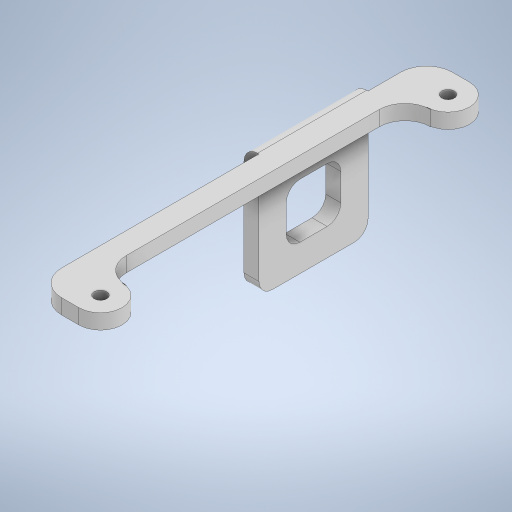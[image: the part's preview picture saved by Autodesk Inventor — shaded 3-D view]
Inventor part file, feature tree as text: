
AUTODESK INVENTOR PART (.ipt)
format: ipt  version: 2023 (Build 270158000, 158)  size: 672,256 bytes
history: native  units: in
note: dims shown in document units (in); Inventor stores cm internally (conversion verified against a paired STEP export)
features: extrude x3, sketch x3, fillet x1
ambient origin geometry x8: Origin, YZ Plane, XZ Plane, XY Plane, X Axis, Y Axis, Z Axis, Center Point
bodies: Solid1 (feature_tree)
feature tree (7):
  extrude  "Extrusion1"  Depth=0.116in
  extrude  "Extrusion2"  Depth=0.395in
  extrude  "Extrusion3"  Depth=0.395in
  fillet  "Fillet1"  Radius=0.2362in
  sketch  "Sketch1"  dims[d0=0.116in d2=0.116in]
  sketch  "Sketch2"  dims[d3=0.395in d4=0.395in]
  sketch  "Sketch4"  dims[d7=3.187in d8=0.395in d9=0.2362in d10=0.2362in d11=0.2362in d12=0.2362in d13=0.1378in d14=0.0in d15=0.3in d16=1.0in d17=1.0in d19=0.25in d22=0.125in d23=0.125in d24=0.125in d25=0.125in d26=0.125in d27=0.125in d28=0.1378in d29=0.0in d30=0.1378in d31=0.0in d32=0.125in d33=3.1096in]
